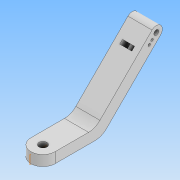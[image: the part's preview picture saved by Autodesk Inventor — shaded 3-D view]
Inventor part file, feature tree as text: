
AUTODESK INVENTOR PART (.ipt)
format: ipt  version: 2021 (Build 250183000, 183)  size: 146,944 bytes
history: native  units: mm
features: other x4, extrude x4, sketch x4, plane x1, fillet x1
ambient origin geometry x8: Origin, YZ Plane, XZ Plane, XY Plane, X Axis, Y Axis, Z Axis, Center Point
bodies: Body1 (feature_tree)
feature tree (14):
  other  "實體1"
  extrude  "擠出1"  Depth=130.0mm TaperAngle=0.0deg
  plane  "工作平面1"
  extrude  "擠出2"  Depth=500.0mm
  extrude  "擠出3"  Depth=1000.0mm
  fillet  "圓角1"  Radius=150.0mm
  extrude  "擠出4"  TaperAngle=45.0deg  [1 undecoded]
  sketch  "草圖1"
  sketch  "草圖2"
  sketch  "草圖3"
  sketch  "草圖4"
  other  "投影切割邊1"
  other  "投影切割邊2"
  other  "投影切割邊3"
note: 1 required parameter value undecoded (feature->parameter linkage not recoverable at this tier; creation-order binding heuristic only, values carry confidence <= 0.55)
